# Revit family: NBS_BilcoUKLtd_FlrHtchs_FloorAccessDrainageDoorTypeJD-ALH20
name_source: partatom
category: Doors
revit_build: Autodesk Revit 2014 (Build: 20130709_2115(x64)
units: mm (PartAtom-declared; Revit-internal decimal feet)

## types (1)
- FloorAccessDrainageDoorTypeJD-1ALH20
    Accessories = Many accessories available
    AssetType = Fixed
    BIMObjectName = NBS_BilcoUKLtd_FloorHatches_FloorAccessDrainageDoorTypeJD-1ALH20
    Category = Pr_30_59_36_30 : Floor hatches
    CutPosition = 1220 mm  [stored 4.00262 ft]
    Description = Double leaf aluminium floor access drainage door
    DoorLoadCapacity = ASHTO H-20 wheel loading (14500 kg axle load)
    DoorMaterial = 6.3 mm thick aluminium reinforced diamond-pattern tread plate
    DoorOrientation = Horizontal
    DoorPosition = Flush
    DurationUnit = year
    Features = Constructed with corrosion resistant materials, heavy-duty construction and positive latching mechanism help to prevent unauthorized access, adjustable anchor tabs, 38 mm drain coupling welded beneath the frame
    FinishOptions = Anodized, Mill (standard)
    FireExit = Yes
    Format = External
    Frame/MullionMaterial = NBS_Concept
    FrameSeal = Yes
    GlazingAreaFraction = 0
    HandicapAccessible = No
    Hardware = Type 316 (1.4401) stainless steel hinge pins, rigid hold open arm
    HardwareFinish = NBS_Concept
    HasDrive = No
    IBeamElevation = -69 mm
    IfcExportAs = IfcDoor
    IfcExportType = NOTDEFINED
    Infiltration = 0
    InternalSize = 1220 x 760 mm (l x w)
    IsExternal = Yes
    LiftingMechanismHeight = 292 mm  [stored 0.958005 ft]
    LockingOptions = Cylinder lock with keyway, Recessed padlock hasp, Security cover McGuard plugs, Stainless steel slam lock (standard)
    ManufacturerName = Bilco UK Ltd
    ManufacturerURL = www.bilcouk.com
    Material = Aluminium
    MiddleSupportBeams = No
    ModelNumber = JD-1AL H20
    ModelReference = Floor Access Drainage Door Type JD-1AL H20
    NBSCertification = http://www.nationalbimlibrary.com
    NBSDescription = Floor hatches
    NBSReference = 45-25-28/420
    Name = FloorHatches_FloorAccessDrainageDoorTypeJD-1ALH20_BilcoUKLtd
    NominalHeight = 305 mm
    NominalLength = 1372 mm  [stored 4.50131 ft]
    NominalWidth = 1014 mm
    OperatingMechanism = Compression spring operators enclosed in telescopic tubes (manual)
    OperationControl = manual
    OperationModeOptions = Manual with fixed interior handle and removable exterior turn/lift handle (standard), Manual with panic latch
    PanelMaterial = NBS_Concept
    ProductInformation = www.bilcouk.com
    SecurityRating = TRUE
    SelfClosing = No
    Shape = Rectangular
    Size = 1372 x 1014 mm
    SmokeStop = Yes
    StructuralOpeningLength = 1220 mm  [stored 4.00262 ft]
    StructuralOpeningWidth = 760 mm
    ThermalTransmittance = 0
    Uniclass2 = 45-60-36/430
    Uniclass2015Description = Floor hatches
    Uniclass2015Reference = Pr_30_59_36_30
    Uniclass2015Version = Products v1.1
    Version = 1
    WarrantyDescription = manufacturer warranty
    WarrantyDurationParts = 25
    WarrantyDurationUnit = year
    Weight = 91 kg

note: [stored X ft] marks values corroborated as IEEE doubles in the binary element streams (Revit-internal decimal feet)

## geometry (parser evidence)
native form markers: Sweep x10
no freeform markers — native parametric forms only
